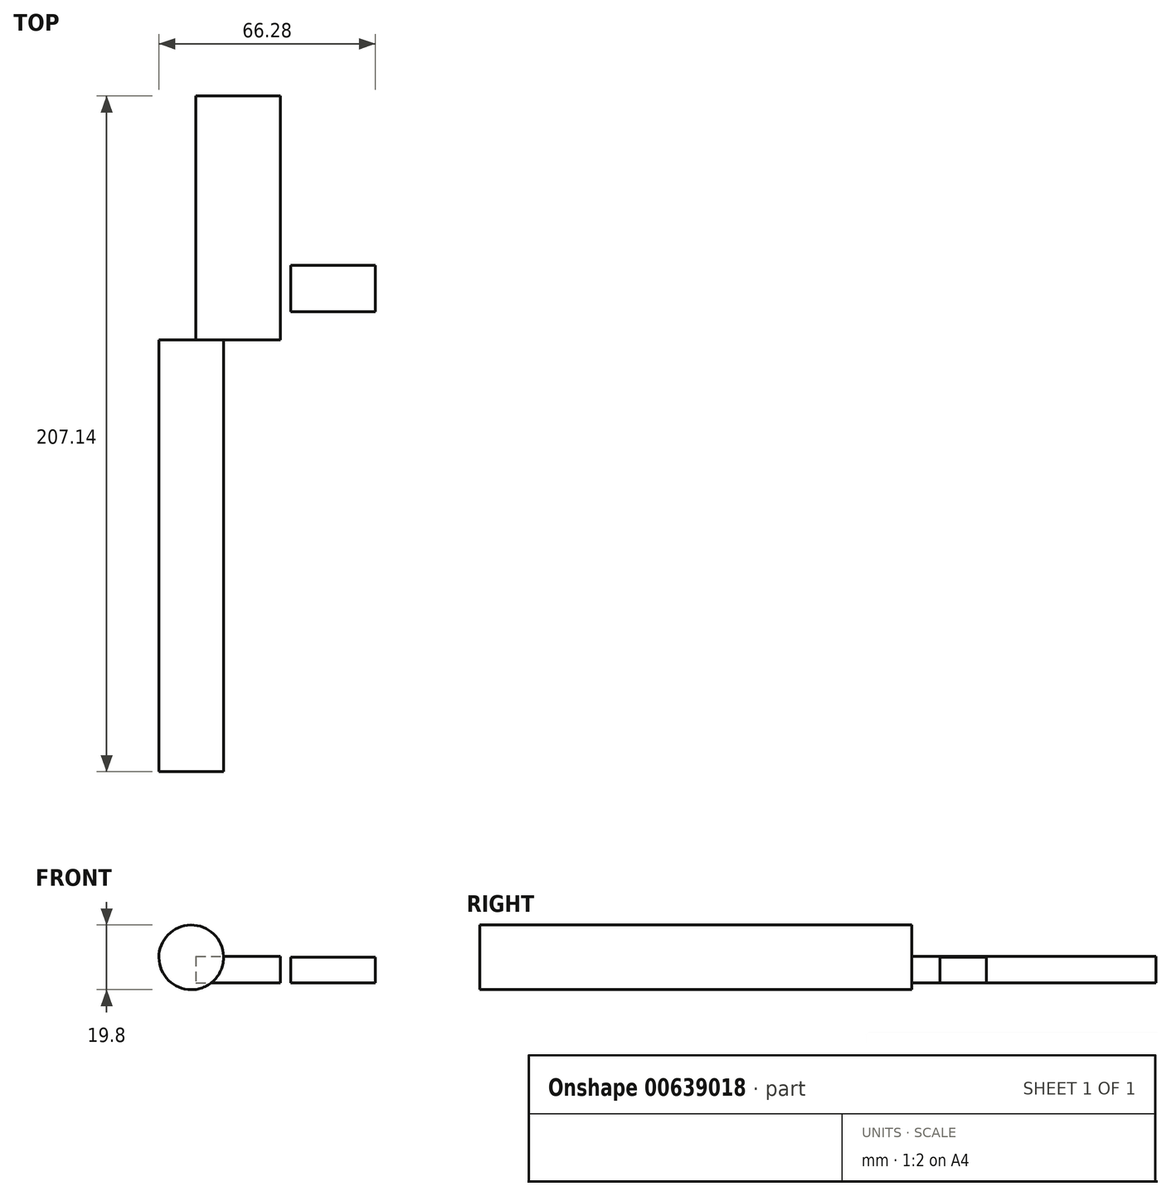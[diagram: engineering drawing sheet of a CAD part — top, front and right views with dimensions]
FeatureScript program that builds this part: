
annotation { "Feature Type Name" : "Feature", "Feature Type Description" : "" }
export const myFeature = defineFeature(function(context is Context, id is Id, definition is map)
    precondition{}
    {
        {
            var Q0;
            Q0=qCreatedBy(makeId("Top.planeOp"),FACE);
            var sketch = newSketch(context, id + "F0", { "sketchPlane" : qUnion([Q0])});
            skLineSegment(sketch, "E0.bottom", {"start": v(0, 0) * mm, "end": v(18.73, 0) * mm});
            skLineSegment(sketch, "E0.top", {"start": v(0, 37.5) * mm, "end": v(18.73, 37.5) * mm});
            skLineSegment(sketch, "E0.left", {"start": v(0, 0) * mm, "end": v(0, 37.5) * mm});
            skLineSegment(sketch, "E0.right", {"start": v(18.73, 0) * mm, "end": v(18.73, 37.5) * mm});
            skLineSegment(sketch, "E1.bottom", {"start": v(18.73, 37.5) * mm, "end": v(5.32, 37.5) * mm});
            skLineSegment(sketch, "E1.top", {"start": v(18.73, 58.75) * mm, "end": v(5.32, 58.75) * mm});
            skLineSegment(sketch, "E1.left", {"start": v(18.73, 37.5) * mm, "end": v(18.73, 58.75) * mm});
            skLineSegment(sketch, "E1.right", {"start": v(5.32, 37.5) * mm, "end": v(5.32, 58.75) * mm});
            skSolve(sketch);
        }
        {
            var Q0;
            Q0=qCreatedBy(makeId("Front.planeOp"),FACE);
            var sketch = newSketch(context, id + "F1", { "sketchPlane" : qUnion([Q0])});
            skCircle(sketch, "E2", {"center": v(-1.44, 0) * mm, "radius": 9.9 * mm});
            skSolve(sketch);
        }
        {
            var Q0;
            Q0=makeQuery(id+"F1.imprint","IMPRINT",FACE,{"disambiguationData":[TD([[makeQuery(id+"F1.imprint","IMPRINT",EDGE,{"derivedFrom":sQuery(id+"F1.wireOp",EDGE,"E2")}),1.0]])]});
            extrude(context, id + "F2", {"entities" : qUnion([Q0]), "depth" : 132.33 * mm, "offsetDistance" : 25.4 * mm});
        }
        {
            var Q0;
            Q0=sQuery(id+"F0.wireOp",EDGE,"E0.right");
            var Q1;
            Q1=sQuery(id+"F0.wireOp",EDGE,"E0.left");
            var Q2;
            Q2=sQuery(id+"F0.wireOp",EDGE,"E0.bottom");
            var Q3;
            Q3=sQuery(id+"F0.wireOp",EDGE,"E1.bottom");
            extrude(context, id + "F3", {"bodyType" : ToolBodyType.SURFACE, "surfaceEntities" : qUnion([Q0, Q1, Q2, Q3]), "depth" : 8.38 * mm, "offsetDistance" : 25.4 * mm});
        }
        {
            var Q0;
            Q0=qCreatedBy(makeId("Top.planeOp"),FACE);
            var sketch = newSketch(context, id + "F4", { "sketchPlane" : qUnion([Q0])});
            skLineSegment(sketch, "E3.bottom", {"start": v(0, 0) * mm, "end": v(25.93, 0) * mm});
            skLineSegment(sketch, "E3.top", {"start": v(0, 74.81) * mm, "end": v(25.93, 74.81) * mm});
            skLineSegment(sketch, "E3.left", {"start": v(0, 0) * mm, "end": v(0, 74.81) * mm});
            skLineSegment(sketch, "E3.right", {"start": v(25.93, 0) * mm, "end": v(25.93, 74.81) * mm});
            skSolve(sketch);
        }
        {
            var Q0;
            Q0=makeQuery(id+"F4.imprint","IMPRINT",FACE,{"disambiguationData":[TD([[makeQuery(id+"F4.imprint","IMPRINT",EDGE,{"derivedFrom":sQuery(id+"F4.wireOp",EDGE,"E3.bottom")}),1.0]])]});
            extrude(context, id + "F5", {"entities" : qUnion([Q0]), "operationType" : NewBodyOperationType.ADD, "depth" : 0.25 * mm, "offsetDistance" : 25.4 * mm});
        }
        {
            var Q0;
            Q0=qCreatedBy(makeId("Top.planeOp"),FACE);
            var sketch = newSketch(context, id + "F6", { "sketchPlane" : qUnion([Q0])});
            skLineSegment(sketch, "E4.bottom", {"start": v(29, 22.94) * mm, "end": v(54.93, 22.94) * mm});
            skLineSegment(sketch, "E4.top", {"start": v(29, 8.63) * mm, "end": v(54.93, 8.63) * mm});
            skLineSegment(sketch, "E4.left", {"start": v(29, 22.94) * mm, "end": v(29, 8.63) * mm});
            skLineSegment(sketch, "E4.right", {"start": v(54.93, 22.94) * mm, "end": v(54.93, 8.63) * mm});
            skSolve(sketch);
        }
        {
            var Q0;
            Q0=makeQuery(id+"F6.imprint","IMPRINT",FACE,{"disambiguationData":[TD([[makeQuery(id+"F6.imprint","IMPRINT",EDGE,{"derivedFrom":sQuery(id+"F6.wireOp",EDGE,"E4.bottom")}),-1.0]])]});
            var Q1;
            Q1=makeQuery(id+"F5.opExtrude","CAP_FACE",FACE,{"disambiguationData":[OSD([sQuery(id+"F4.wireOp",EDGE,"E3.bottom"),sQuery(id+"F4.wireOp",EDGE,"E3.top"),sQuery(id+"F4.wireOp",EDGE,"E3.left"),sQuery(id+"F4.wireOp",EDGE,"E3.right")])],"isStart":true});
            var Q2;
            Q2=makeQuery(id+"F5.opExtrude","CAP_FACE",FACE,{"disambiguationData":[OSD([sQuery(id+"F4.wireOp",EDGE,"E3.bottom"),sQuery(id+"F4.wireOp",EDGE,"E3.top"),sQuery(id+"F4.wireOp",EDGE,"E3.left"),sQuery(id+"F4.wireOp",EDGE,"E3.right")])],"isStart":false});
            extrude(context, id + "F7", {"entities" : qUnion([Q0, Q1, Q2]), "operationType" : NewBodyOperationType.ADD, "oppositeDirection" : true, "depth" : 7.87 * mm, "offsetDistance" : 25.4 * mm});
        }
    });
